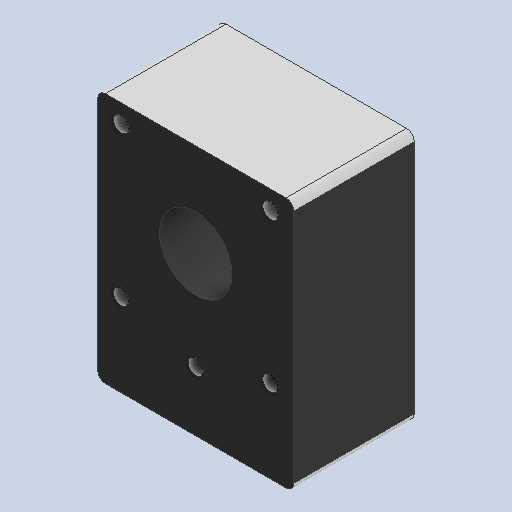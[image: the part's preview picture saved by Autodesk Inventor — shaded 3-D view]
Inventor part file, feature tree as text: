
AUTODESK INVENTOR PART (.ipt)
format: ipt  version: 2025.1 (Build 291241020, 241B)  size: 230,912 bytes
history: native  units: in
note: dims shown in document units (in); Inventor stores cm internally (conversion verified against a paired STEP export)
features: extrude x3, sketch x3, fillet x1
ambient origin geometry x8: Origin, YZ Plane, XZ Plane, XY Plane, X Axis, Y Axis, Z Axis, Center Point
bodies: Solid1 (feature_tree)
feature tree (7):
  extrude  "Extrusion1"  Depth=1.6in
  extrude  "Extrusion2"  Depth=0.9843in
  extrude  "Extrusion3"  Depth=0.063in TaperAngle=0.0deg
  fillet  "Fillet1"  Radius=0.125in
  sketch  "Sketch1"  dims[d0=1.6in d1=2.1in]
  sketch  "Sketch2"  dims[d2=0.9843in d3=0.0in d4=0.8125in]
  sketch  "Sketch3"  dims[d5=0.5906in d6=0.5in d7=0.0in d8=0.125in d9=0.8in d11=0.125in d12=0.6102in d13=0.6102in d14=0.05in d15=0.0in d16=0.063in]
